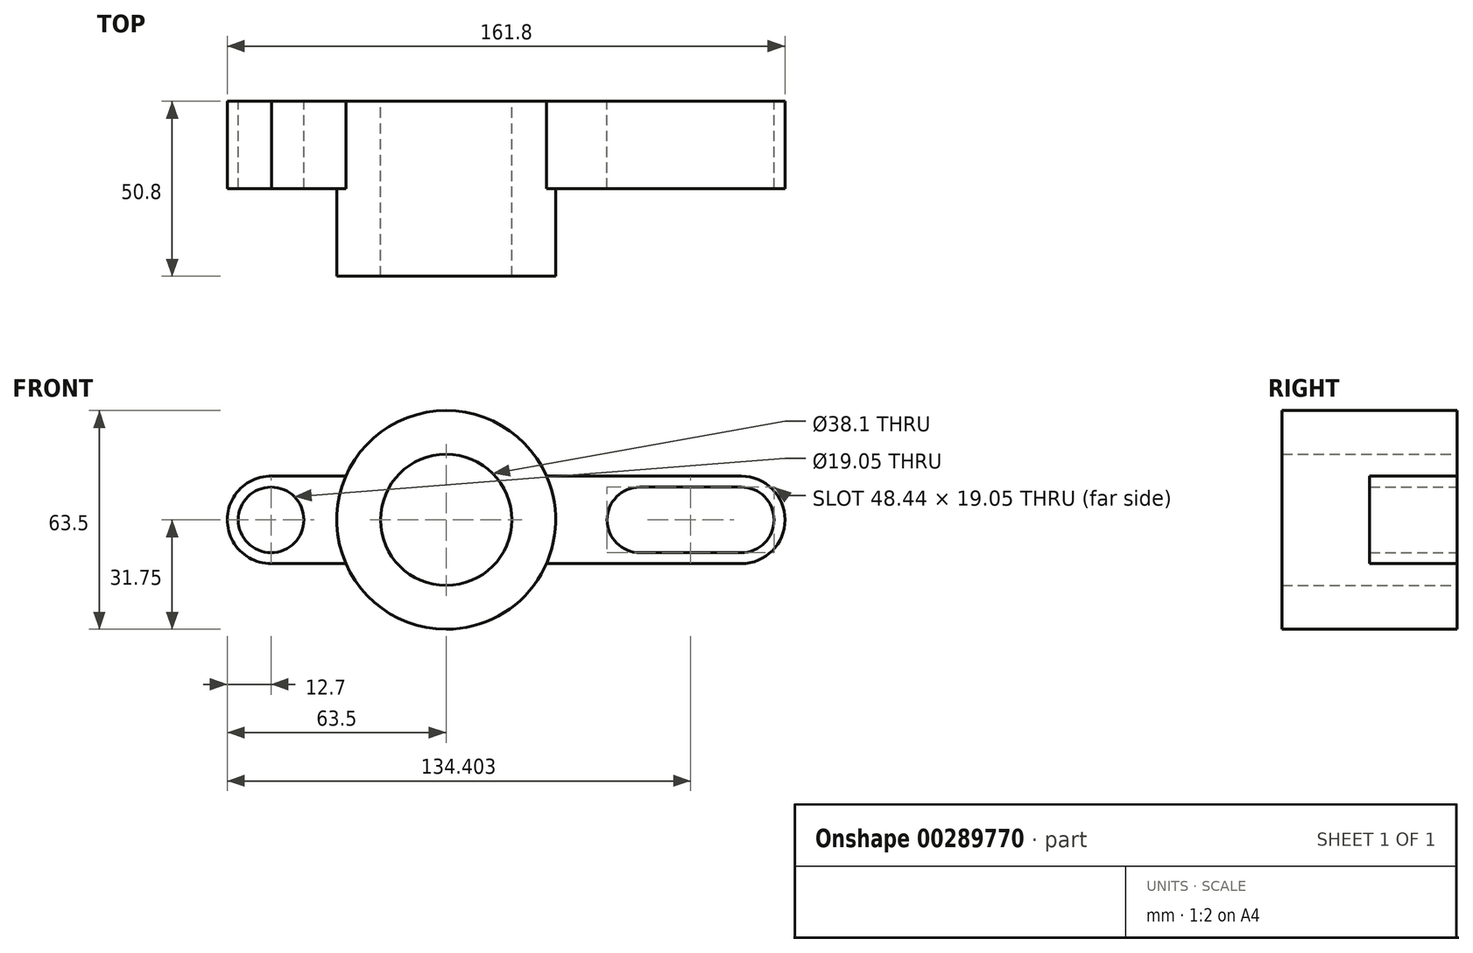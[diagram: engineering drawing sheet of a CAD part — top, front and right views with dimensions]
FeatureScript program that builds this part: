
annotation { "Feature Type Name" : "Feature", "Feature Type Description" : "" }
export const myFeature = defineFeature(function(context is Context, id is Id, definition is map)
    precondition{}
    {
        {
            var Q0;
            Q0=qCreatedBy(makeId("Front.planeOp"),FACE);
            var sketch = newSketch(context, id + "F0", { "sketchPlane" : qUnion([Q0])});
            skCircle(sketch, "E0", {"center": v(0, 0) * mm, "radius": 12.7 * mm});
            skCircle(sketch, "E1", {"center": v(0, 0) * mm, "radius": 19.05 * mm});
            skCircle(sketch, "E2", {"center": v(0, 0) * mm, "radius": 31.75 * mm});
            skArc(sketch, "E3", {"start": v(-50.6, 12.7) * mm, "mid": v(-63.5, 0.1) * mm, "end": v(-50.8, -12.7) * mm});
            skArc(sketch, "E4", {"start": v(85.6, -12.7) * mm, "mid": v(98.3, 0) * mm, "end": v(85.6, 12.7) * mm});
            skLineSegment(sketch, "E5", {"start": v(-51, 12.7) * mm, "end": v(-29.1, 12.7) * mm});
            skLineSegment(sketch, "E6", {"start": v(-50.8, -12.7) * mm, "end": v(-29.1, -12.7) * mm});
            skLineSegment(sketch, "E7", {"start": v(85.6, 12.7) * mm, "end": v(29.1, 12.7) * mm});
            skLineSegment(sketch, "E8", {"start": v(85.6, -12.7) * mm, "end": v(29.1, -12.7) * mm});
            skCircle(sketch, "E9", {"center": v(-50.8, 0) * mm, "radius": 9.53 * mm});
            skArc(sketch, "E10", {"start": v(56.2, 9.53) * mm, "mid": v(46.68, 0) * mm, "end": v(56.2, -9.53) * mm});
            skArc(sketch, "E11", {"start": v(85.6, -9.52) * mm, "mid": v(95.12, 0) * mm, "end": v(85.6, 9.53) * mm});
            skLineSegment(sketch, "E12", {"start": v(56.2, 9.53) * mm, "end": v(85.6, 9.53) * mm});
            skLineSegment(sketch, "E13", {"start": v(56.2, -9.53) * mm, "end": v(85.6, -9.53) * mm});
            skSolve(sketch);
        }
        {
            var Q0;
            Q0=makeQuery(id+"F0.imprint","IMPRINT",FACE,{"disambiguationData":[TD([[makeQuery(id+"F0.imprint","IMPRINT",EDGE,{"derivedFrom":sQuery(id+"F0.wireOp",EDGE,"E1")}),-1.0]])]});
            extrude(context, id + "F1", {"entities" : qUnion([Q0]), "depth" : 50.8 * mm});
        }
        {
            var Q0;
            {var subQ6=sQuery(id+"F0.wireOp",EDGE,"E6");Q0=makeQuery(id+"F0.imprint","IMPRINT",FACE,{"disambiguationData":[TD([[makeQuery(id+"F0.imprint","IMPRINT",EDGE,{"derivedFrom":subQ6}),1.0]])]});}
            extrude(context, id + "F2", {"entities" : qUnion([Q0]), "operationType" : NewBodyOperationType.ADD, "depth" : 19.05 * mm});
        }
        {
            var Q0;
            Q0 = qSketchRegion(id + "F0", true);
            extrude(context, id + "F3", {"entities" : qUnion([Q0]), "operationType" : NewBodyOperationType.ADD, "depth" : 25.4 * mm});
        }
        {
            var Q0;
            Q0 = qSketchRegion(id + "F0", true);
            extrude(context, id + "F4", {"entities" : qUnion([Q0]), "operationType" : NewBodyOperationType.ADD, "depth" : 25.4 * mm});
        }
    });
